FCSTD DOCUMENT  (FreeCAD 0.20R29177 +426 (Git))
Label: Test
License: All rights reserved
LicenseURL: http://en.wikipedia.org/wiki/All_rights_reserved
objects: Sketcher::SketchObject×2, Spreadsheet::Sheet×1, PartDesign::Body×1
note: 3 computed .brp shape members not serialized (recipe doc carries the construction recipe); baked Part::Feature solids carry a one-line shape summary decoded from their .brp

FEATURE [Spreadsheet::Sheet] Spreadsheet
  cells = A1=Inputs; C1=Test (from Radius); E1=Computed (HoopWise); G1=Computed (HoopWise); A2=Angle; B2(Angle)=15; C2=Test Radius; D2(TestRadius)=5.892; E2=Radius; F2(Radius)==(AnchorX + tan(Angle) * AnchorY) / (cos(Angle) + tan(Angle) + tan(Angle) * sin(Angle)); G2=Radius; H2(hwRadius)==Segment / 2 - Thickness / 2; A3=Thickness; B3(Thickness)=2; C3=ArcX; D3(TestArcX)==TestRadius - cos(Angle) * TestRadius; E3=ArcX; F3(ArcX)==Radius - cos(Angle) * Radius; G3=ArcX; H3(hwArcX)==hwRadius - cos(Angle) * hwRadius; A4=Length; B4(Length)=50; C4=ArcY; D4(TestArcY)==sin(Angle) * TestRadius; E4=ArcY; F4(ArcY)==sin(Angle) * Radius; G4=ArcY; H4(hwArcY)==sin(Angle) * hwRadius; A5=Width; B5(Width)=20; C5=ArmX; D5(TestArmX)==tan(Angle) * TestArmY; E5=ArmX; F5(ArmX)==tan(Angle) * ArmY; G5=ArmX; H5(hwArmX)==tan(Angle) * hwArmY; A6=Frequency; B6(Frequency)=5; C6=ArmY; D6(TestArmY)==Width / 2 - 5.892 - sin(Angle) * TestRadius; E6=ArmY; F6(ArmY)==AnchorY - Radius - sin(Angle) * Radius; G6=ArmY; H6(hwArmY)==Width / 2 - Thickness / 2 - hwRadius - hwArcY; A7=Depth; B7(Depth)=5; A8=Segment; B8(Segment)==Length / Frequency; E8=AnchorX; F8(AnchorX)==Segment / 2; G8=AnchorX; H8(hwAnchorX)==Segment / 2; E9=AnchorY; F9(AnchorY)==Width / 2 - Thickness / 2; G9=AnchorY; H9(hwAnchorY)==Width / 2 - Thickness / 2; G11=ArmOffsetX; H11(hwOffsetX)==Segment / 2 - hwRadius + hwArmX + hwArcX; G12=ArmOffsetY; H12(hwOffsetY)=
FEATURE [Sketcher::SketchObject] Sketch001  label="RungWiseSketch"
  FullyConstrained = true
  MapMode = 5
  Support = -> [XY_Plane]
  expr: Constraints[10] = Spreadsheet.Segment / 2
  expr: Constraints[11] = Spreadsheet.Width / 2
  expr: Constraints[13] = Spreadsheet.Angle
  expr: Constraints[39] = Spreadsheet.AnchorX
  expr: Constraints[40] = Spreadsheet.AnchorY
  expr: Constraints[41] = 90 + Spreadsheet.Angle
  expr: Constraints[42] = Spreadsheet.Radius
  expr: Constraints[8] = Spreadsheet.Width
  expr: Constraints[9] = Spreadsheet.Segment
  sketch-geometry (12):
    g0: LineSegment StartX=5 StartY=10 StartZ=0 EndX=-5 EndY=10 EndZ=0
    g1: LineSegment StartX=-5 StartY=10 StartZ=0 EndX=-5 EndY=-10 EndZ=0
    g2: LineSegment StartX=-5 StartY=-10 StartZ=0 EndX=5 EndY=-10 EndZ=0
    g3: LineSegment StartX=5 StartY=-10 StartZ=0 EndX=5 EndY=10 EndZ=0
    g4: LineSegment StartX=0 StartY=0 StartZ=0 EndX=-0.691893 EndY=2.58218 EndZ=0
    g5: ArcOfCircle CenterX=5 CenterY=4.10732 CenterZ=0 NormalX=0 NormalY=0 NormalZ=1 AngleXU=0 Radius=5.89268 StartAngle=1.5708 EndAngle=3.40339
    g6: LineSegment StartX=5 StartY=4.10732 StartZ=0 EndX=-0.892681 EndY=4.10732 EndZ=0
    g7: LineSegment StartX=-0.691893 StartY=2.58218 StartZ=0 EndX=5 EndY=4.10732 EndZ=0
    g8: ArcOfCircle CenterX=5 CenterY=3.31292 CenterZ=0 NormalX=0 NormalY=0 NormalZ=1 AngleXU=0 Radius=5.68708 StartAngle=1.5708 EndAngle=3.40339
    g9: LineSegment StartX=5 StartY=10 StartZ=0 EndX=5 EndY=9 EndZ=0
    g10: LineSegment StartX=5 StartY=9 StartZ=0 EndX=5 EndY=8 EndZ=0
    g11: LineSegment StartX=5 StartY=9 StartZ=0 EndX=5 EndY=0 EndZ=0
  constraints (43):
    c: Coincident(g0,g1)
    c: Coincident(g1,g2)
    c: Coincident(g2,g3)
    c: Coincident(g3,g0)
    c: Horizontal(g0)
    c: Horizontal(g2)
    c: Vertical(g1)
    c: Vertical(g3)
    c: DistanceY(g3,g3) = 20
    c: DistanceX(g0,g0) = 10
    c: DistanceX(g0,g-1) = 5
    c: DistanceY(g2,g-1) = 10
    c: Coincident(g4,g-1)
    c: Angle(g-2,g4) = 0.261799
    c: Tangent(g5,g0) = -1.5708
    c: DistanceX(g5,g0) = 0
    c: Radius(g5) = 5.89268
    c: Tangent(g4,g5) = 1.5708
    c: DistanceY(g4,g4) = 2.58218
    c: DistanceX(g4,g4) = 0.691893
    c: Coincident(g6,g5)
    c: PointOnObject(g6,g5)
    c: Horizontal(g6)
    c: Coincident(g7,g4)
    c: Coincident(g7,g5)
    c: DistanceY(g4,g4) = 2.58218
    c: DistanceY(g4,g6) = 1.52514
    c: DistanceX(g6,g4) = 0.200788
    c: Coincident(g9,g10)
    c: Distance(g9,g10) = 2
    c: Perpendicular(g8,g9)
    c: Perpendicular(g8,g10)
    c: Equal(g10,g9)
    c: PointOnObject(g9,g8)
    c: Coincident(g11,g8)
    c: PointOnObject(g11,g-1)
    c: Vertical(g11)
    c: Perpendicular(g8,g11)
    c: DistanceX(g9,g8) = 0
    c: DistanceX(g4,g8) = 5
    c: DistanceY(g4,g8) = 9
    c: Angle(g8) = 1.8326
    c: Radius(g8) = 5.68708
FEATURE [Sketcher::SketchObject] Sketch  label="HoopWiseSketch"
  FullyConstrained = false
  MapMode = 5
  Support = -> [XY_Plane]
  expr: Constraints[10] = Spreadsheet.Segment
  expr: Constraints[11] = Spreadsheet.Segment / 2
  expr: Constraints[12] = 90 + Spreadsheet.Angle
  expr: Constraints[13] = Spreadsheet.hwRadius
  expr: Constraints[18] = Spreadsheet.hwAnchorY
  expr: Constraints[19] = Spreadsheet.hwAnchorX
  expr: Constraints[25] = Spreadsheet.Thickness / 2
  expr: Constraints[29] = Spreadsheet.Angle
  expr: Constraints[37] = Spreadsheet.hwArmY
  expr: Constraints[39] = Spreadsheet.hwArmX
  expr: Constraints[8] = Spreadsheet.Width
  expr: Constraints[9] = Spreadsheet.Width / 2
  sketch-geometry (12):
    g0: LineSegment StartX=-5 StartY=10 StartZ=0 EndX=5 EndY=10 EndZ=0
    g1: LineSegment StartX=5 StartY=10 StartZ=0 EndX=5 EndY=-10 EndZ=0
    g2: LineSegment StartX=5 StartY=-10 StartZ=0 EndX=-5 EndY=-10 EndZ=0
    g3: LineSegment StartX=-5 StartY=-10 StartZ=0 EndX=-5 EndY=10 EndZ=0
    g4: ArcOfCircle CenterX=5 CenterY=5 CenterZ=0 NormalX=0 NormalY=0 NormalZ=1 AngleXU=0 Radius=4 StartAngle=1.5708 EndAngle=3.40339
    g5: LineSegment StartX=5 StartY=9 StartZ=0 EndX=5 EndY=0 EndZ=0
    g6: LineSegment StartX=2.7092 StartY=9.44435 StartZ=0 EndX=3.16736 EndY=8.55548 EndZ=0
    g7: LineSegment StartX=3.16736 StartY=8.55548 StartZ=0 EndX=3.62552 EndY=7.66661 EndZ=0
    g8: LineSegment StartX=1.1363 StartY=3.96472 StartZ=0 EndX=2.19864 EndY=0 EndZ=0
    g9: LineSegment StartX=2.19864 StartY=0 StartZ=0 EndX=2.19864 EndY=3.96472 EndZ=0
    g10: LineSegment StartX=5 StartY=5 StartZ=0 EndX=1 EndY=5 EndZ=0
    g11: LineSegment StartX=1.1363 StartY=3.96472 StartZ=0 EndX=5 EndY=5 EndZ=0
  constraints (41):
    c: Coincident(g0,g1)
    c: Coincident(g1,g2)
    c: Coincident(g2,g3)
    c: Coincident(g3,g0)
    c: Horizontal(g0)
    c: Horizontal(g2)
    c: Vertical(g1)
    c: Vertical(g3)
    c: DistanceY(g1,g1) = 20
    c: DistanceY(g-1,g0) = 10
    c: DistanceX(g0,g0) = 10
    c: DistanceX(g0,g-1) = 5
    c: Angle(g4) = 1.8326
    c: Radius(g4) = 4
    c: Coincident(g5,g4)
    c: PointOnObject(g5,g-1)
    c: Vertical(g5)
    c: Perpendicular(g4,g5)
    c: DistanceY(g-1,g4) = 9
    c: DistanceX(g-1,g4) = 5
    c: Coincident(g6,g7)
    c: PointOnObject(g6,g4)
    c: Parallel(g6,g7)
    c: Equal(g7,g6)
    c: Perpendicular(g4,g6)
    c: Distance(g7) = 1
    c: Coincident(g9,g8)
    c: Vertical(g9)
    c: Horizontal(g9,g8)
    c: Angle(g9,g8) = 0.261799
    c: Coincident(g10,g4)
    c: PointOnObject(g10,g4)
    c: Horizontal(g10)
    c: Coincident(g11,g4)
    c: Coincident(g11,g4)
    c: DistanceY(g4,g10) = 1.03528
    c: DistanceX(g10,g4) = 0.136297
    c: DistanceY(g8,g8) = 3.96472
    c: DistanceY(g8,g-1) = 0
    c: DistanceX(g4,g8) = 1.06234
    c: DistanceX(g-1,g8) = 2.19864
FEATURE [PartDesign::Body] Body
  Group = -> [Sketch001,Sketch]
  Origin = -> Origin
